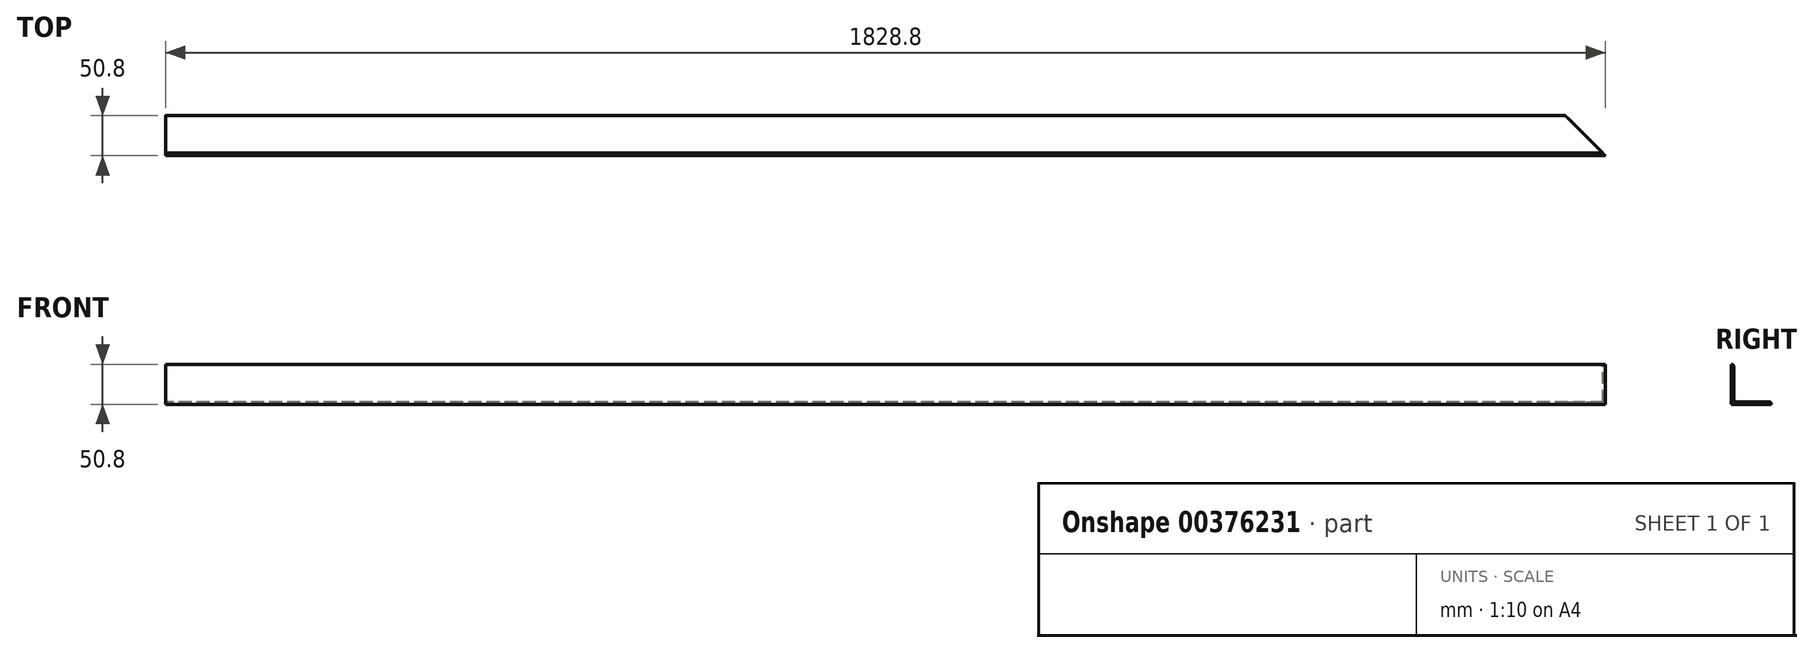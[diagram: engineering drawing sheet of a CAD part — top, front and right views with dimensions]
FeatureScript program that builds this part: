
annotation { "Feature Type Name" : "Feature", "Feature Type Description" : "" }
export const myFeature = defineFeature(function(context is Context, id is Id, definition is map)
    precondition{}
    {
        {
            var Q0;
            Q0=qCreatedBy(makeId("Right.planeOp"),FACE);
            var sketch = newSketch(context, id + "F0", { "sketchPlane" : qUnion([Q0])});
            skLineSegment(sketch, "E0", {"start": v(0, 0) * mm, "end": v(-50.8, 0) * mm});
            skLineSegment(sketch, "E1", {"start": v(-50.8, 0) * mm, "end": v(-50.8, 50.8) * mm});
            skLineSegment(sketch, "E2.0", {"start": v(-47.63, 3.17) * mm, "end": v(-47.63, 47.62) * mm});
            skLineSegment(sketch, "E2.1", {"start": v(-3.18, 3.17) * mm, "end": v(-47.63, 3.17) * mm});
            skLineSegment(sketch, "E3", {"start": v(-50.8, 50.8) * mm, "end": v(-50.8, 50.8) * mm});
            skLineSegment(sketch, "E4", {"start": v(0, 0) * mm, "end": v(0, 0) * mm});
            skPoint(sketch, "E5.visualSharp", {"position": v(-47.63, 50.8) * mm});
            skArc(sketch, "E5.filletArc", {"start": v(-47.63, 47.62) * mm, "mid": v(-48.55, 49.87) * mm, "end": v(-50.8, 50.8) * mm});
            skPoint(sketch, "E6.visualSharp", {"position": v(0, 3.17) * mm});
            skArc(sketch, "E6.filletArc", {"start": v(0, 0) * mm, "mid": v(-0.93, 2.25) * mm, "end": v(-3.18, 3.17) * mm});
            skSolve(sketch);
        }
        {
            var Q0;
            Q0 = qSketchRegion(id + "F0", true);
            extrude(context, id + "F1", {"entities" : qUnion([Q0]), "endBound" : BoundingType.SYMMETRIC, "depth" : 1828.8 * mm});
        }
        {
            var Q0;
            Q0=makeQuery(id+"F1.opExtrude","SWEPT_FACE",FACE,{"disambiguationData":[OSD([sQuery(id+"F0.wireOp",EDGE,"E0")])]});
            var sketch = newSketch(context, id + "F2", { "sketchPlane" : qUnion([Q0])});
            skLineSegment(sketch, "E7", {"start": v(863.6, 0) * mm, "end": v(914.4, 0) * mm});
            skLineSegment(sketch, "E8", {"start": v(863.6, 0) * mm, "end": v(914.4, 50.8) * mm});
            skLineSegment(sketch, "E9", {"start": v(914.4, 50.8) * mm, "end": v(914.4, 0) * mm});
            skSolve(sketch);
        }
        {
            var Q0;
            Q0 = qSketchRegion(id + "F2", true);
            extrude(context, id + "F3", {"entities" : qUnion([Q0]), "operationType" : NewBodyOperationType.REMOVE, "oppositeDirection" : true, "depth" : 76.2 * mm});
        }
    });
